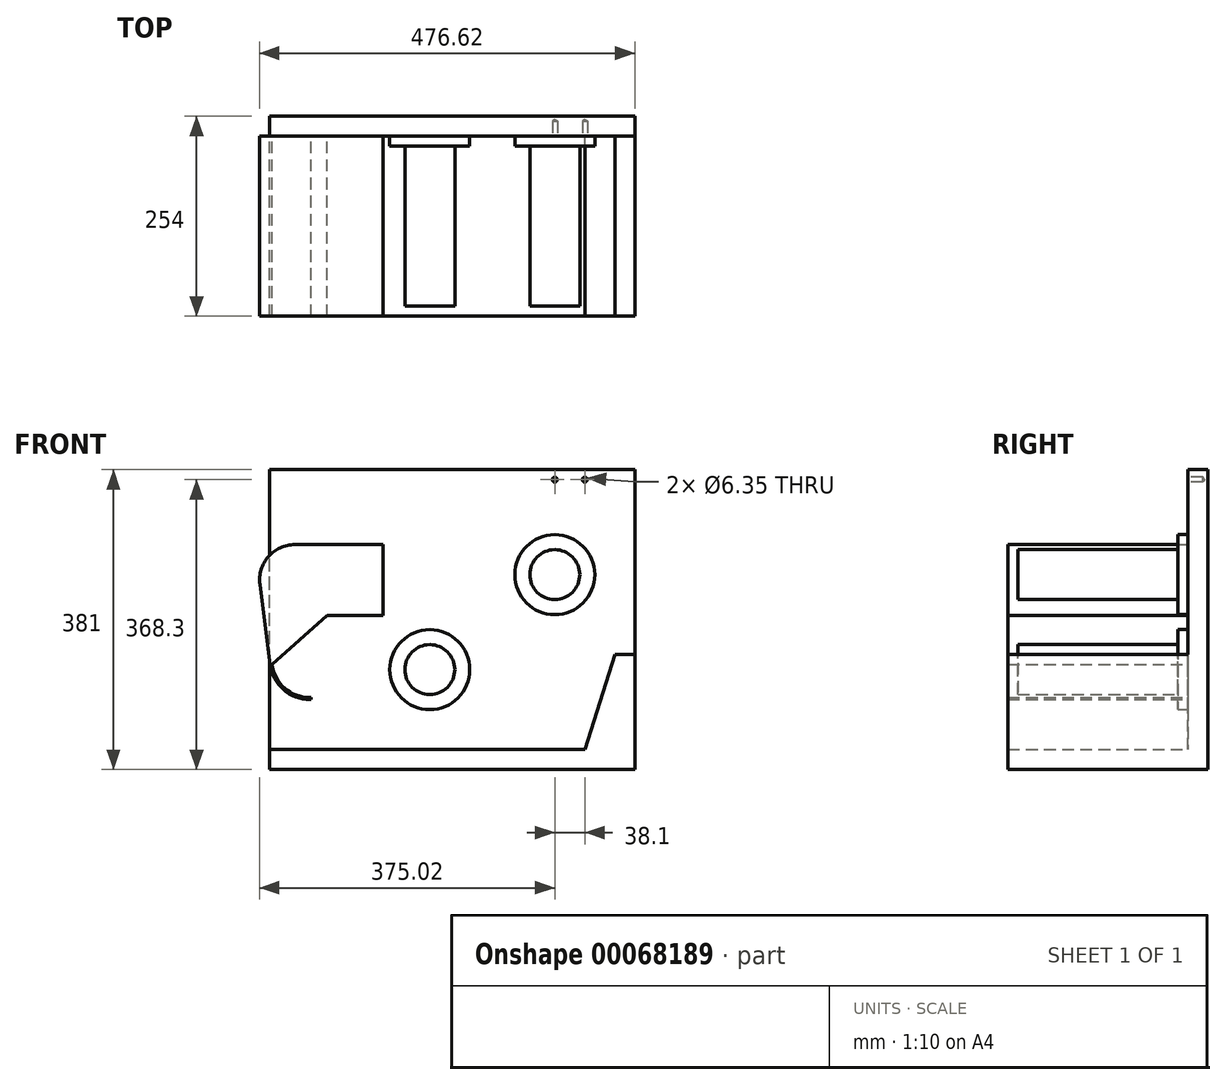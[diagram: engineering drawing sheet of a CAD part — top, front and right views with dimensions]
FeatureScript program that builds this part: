
annotation { "Feature Type Name" : "Feature", "Feature Type Description" : "" }
export const myFeature = defineFeature(function(context is Context, id is Id, definition is map)
    precondition{}
    {
        {
            var Q0;
            Q0=qCreatedBy(makeId("Front.planeOp"),FACE);
            var sketch = newSketch(context, id + "F0", { "sketchPlane" : qUnion([Q0])});
            skLineSegment(sketch, "E0.bottom", {"start": v(0, 0) * mm, "end": v(463.55, 0) * mm});
            skLineSegment(sketch, "E0.top", {"start": v(0, 381) * mm, "end": v(463.55, 381) * mm});
            skLineSegment(sketch, "E0.left", {"start": v(0, 0) * mm, "end": v(0, 381) * mm});
            skLineSegment(sketch, "E0.right", {"start": v(463.55, 0) * mm, "end": v(463.55, 381) * mm});
            skSolve(sketch);
        }
        {
            var Q0;
            Q0=makeQuery(id+"F0.imprint","IMPRINT",FACE,{"disambiguationData":[TD([[makeQuery(id+"F0.imprint","IMPRINT",EDGE,{"derivedFrom":sQuery(id+"F0.wireOp",EDGE,"E0.bottom")}),1.0]])]});
            extrude(context, id + "F1", {"entities" : qUnion([Q0]), "depth" : 25.4 * mm});
        }
        {
            var Q0;
            Q0=makeQuery(id+"F1.opExtrude","CAP_FACE",FACE,{"disambiguationData":[OSD([sQuery(id+"F0.wireOp",EDGE,"E0.bottom"),sQuery(id+"F0.wireOp",EDGE,"E0.top"),sQuery(id+"F0.wireOp",EDGE,"E0.left"),sQuery(id+"F0.wireOp",EDGE,"E0.right")])],"isStart":false});
            var sketch = newSketch(context, id + "F2", { "sketchPlane" : qUnion([Q0])});
            skLineSegment(sketch, "E1.bottom", {"start": v(0, 0) * mm, "end": v(463.55, 0) * mm});
            skLineSegment(sketch, "E1.top", {"start": v(0, 25.4) * mm, "end": v(463.55, 25.4) * mm});
            skLineSegment(sketch, "E1.left", {"start": v(0, 0) * mm, "end": v(0, 25.4) * mm});
            skLineSegment(sketch, "E1.right", {"start": v(463.55, 0) * mm, "end": v(463.55, 25.4) * mm});
            skSolve(sketch);
        }
        {
            var Q0;
            Q0=makeQuery(id+"F2.imprint","IMPRINT",FACE,{"disambiguationData":[TD([[makeQuery(id+"F2.imprint","IMPRINT",EDGE,{"derivedFrom":sQuery(id+"F2.wireOp",EDGE,"E1.bottom")}),1.0]])]});
            extrude(context, id + "F3", {"entities" : qUnion([Q0]), "operationType" : NewBodyOperationType.ADD, "depth" : 228.6 * mm});
        }
        {
            var Q0;
            Q0=makeQuery(id+"F1.opExtrude","CAP_FACE",FACE,{"disambiguationData":[OSD([sQuery(id+"F0.wireOp",EDGE,"E0.bottom"),sQuery(id+"F0.wireOp",EDGE,"E0.top"),sQuery(id+"F0.wireOp",EDGE,"E0.left"),sQuery(id+"F0.wireOp",EDGE,"E0.right")])],"isStart":false});
            var sketch = newSketch(context, id + "F4", { "sketchPlane" : qUnion([Q0])});
            skLineSegment(sketch, "E2", {"start": v(0.41, 133.22) * mm, "end": v(-12.7, 235.22) * mm});
            skArc(sketch, "E3", {"start": v(31.75, 285.75) * mm, "mid": v(-1.9, 270.53) * mm, "end": v(-12.7, 235.22) * mm});
            skArc(sketch, "E4", {"start": v(0.41, 133.22) * mm, "mid": v(17.25, 101.56) * mm, "end": v(50.8, 88.9) * mm});
            skLineSegment(sketch, "E5", {"start": v(31.75, 285.75) * mm, "end": v(144.01, 285.75) * mm});
            skLineSegment(sketch, "E6", {"start": v(144.01, 285.75) * mm, "end": v(144.01, 195.85) * mm});
            skLineSegment(sketch, "E7", {"start": v(144.01, 195.85) * mm, "end": v(72.48, 195.85) * mm});
            skLineSegment(sketch, "E8", {"start": v(50.8, 88.9) * mm, "end": v(50.8, 91.44) * mm});
            skArc(sketch, "E9", {"start": v(2.93, 133.55) * mm, "mid": v(18.93, 103.46) * mm, "end": v(50.8, 91.44) * mm});
            skLineSegment(sketch, "E10", {"start": v(50.8, 88.9) * mm, "end": v(50.8, 139.7) * mm, "construction": true});
            skLineSegment(sketch, "E11", {"start": v(0.41, 133.22) * mm, "end": v(50.8, 139.7) * mm, "construction": true});
            skLineSegment(sketch, "E12", {"start": v(2.93, 133.55) * mm, "end": v(72.48, 195.85) * mm});
            skSolve(sketch);
        }
        {
            var Q0;
            Q0 = qSketchRegion(id + "F4", true);
            var Q1;
            Q1=makeQuery(id+"F4.imprint","IMPRINT",FACE,{"disambiguationData":[TD([[makeQuery(id+"F4.imprint","IMPRINT",EDGE,{"derivedFrom":sQuery(id+"F4.wireOp",EDGE,"E2")}),-1.0]])]});
            extrude(context, id + "F5", {"entities" : qUnion([Q0, Q1]), "operationType" : NewBodyOperationType.ADD, "depth" : 228.6 * mm});
        }
        {
            var Q0;
            Q0=makeQuery(id+"F1.opExtrude","CAP_FACE",FACE,{"disambiguationData":[OSD([sQuery(id+"F0.wireOp",EDGE,"E0.bottom"),sQuery(id+"F0.wireOp",EDGE,"E0.top"),sQuery(id+"F0.wireOp",EDGE,"E0.left"),sQuery(id+"F0.wireOp",EDGE,"E0.right")])],"isStart":false});
            var sketch = newSketch(context, id + "F6", { "sketchPlane" : qUnion([Q0])});
            skPoint(sketch, "E13", {"position": v(361.95, 368.3) * mm});
            skPoint(sketch, "E14", {"position": v(400.05, 368.3) * mm});
            skSolve(sketch);
        }
        {
            var Q0;
            Q0=sQuery(id+"F6.wireOp",VERTEX,"E13");
            var Q1;
            Q1=sQuery(id+"F6.wireOp",VERTEX,"E14");
            var Q2;
            Q2=makeQuery(id+"F1.opExtrude","SWEPT_BODY",BODY,{"disambiguationData":[OSD([sQuery(id+"F0.wireOp",EDGE,"E0.bottom"),sQuery(id+"F0.wireOp",EDGE,"E0.top"),sQuery(id+"F0.wireOp",EDGE,"E0.left"),sQuery(id+"F0.wireOp",EDGE,"E0.right")])]});
            hole(context, id + "F7", {"style" : HoleStyle.SIMPLE, "holeDiameter" : 6.35 * mm, "endStyle" : HoleEndStyle.BLIND, "holeDepth" : 19.05 * mm, "locations" : qUnion([Q0, Q1]), "scope" : qUnion([Q2])});
        }
        {
            var Q0;
            Q0=makeQuery(id+"F5.opExtrude","SWEPT_FACE",FACE,{"disambiguationData":[OSD([sQuery(id+"F4.wireOp",EDGE,"E8")])]});
            extrude(context, id + "F8", {"entities" : qUnion([Q0]), "operationType" : NewBodyOperationType.ADD, "depth" : (1 + (7 / 8)) * mm});
        }
        {
            var Q0;
            Q0=makeQuery(id+"F1.opExtrude","CAP_FACE",FACE,{"disambiguationData":[OSD([sQuery(id+"F0.wireOp",EDGE,"E0.bottom"),sQuery(id+"F0.wireOp",EDGE,"E0.top"),sQuery(id+"F0.wireOp",EDGE,"E0.left"),sQuery(id+"F0.wireOp",EDGE,"E0.right")])],"isStart":false});
            var sketch = newSketch(context, id + "F9", { "sketchPlane" : qUnion([Q0])});
            skCircle(sketch, "E15", {"center": v(203.2, 127) * mm, "radius": 50.8 * mm});
            skSolve(sketch);
        }
        {
            var Q0;
            Q0 = qSketchRegion(id + "F9", true);
            extrude(context, id + "F10", {"entities" : qUnion([Q0]), "operationType" : NewBodyOperationType.ADD, "depth" : 12.7 * mm});
        }
        {
            var Q0;
            Q0=makeQuery(id+"F10.opExtrude","CAP_FACE",FACE,{"disambiguationData":[OSD([sQuery(id+"F9.wireOp",EDGE,"E15")])],"isStart":false});
            var sketch = newSketch(context, id + "F11", { "sketchPlane" : qUnion([Q0])});
            skCircle(sketch, "E16", {"center": v(203.2, 127) * mm, "radius": 31.75 * mm});
            skSolve(sketch);
        }
        {
            var Q0;
            Q0 = qSketchRegion(id + "F11", true);
            extrude(context, id + "F12", {"entities" : qUnion([Q0]), "operationType" : NewBodyOperationType.ADD, "depth" : 203.2 * mm});
        }
        {
            var Q0;
            Q0=makeQuery(id+"F1.opExtrude","CAP_FACE",FACE,{"disambiguationData":[OSD([sQuery(id+"F0.wireOp",EDGE,"E0.bottom"),sQuery(id+"F0.wireOp",EDGE,"E0.top"),sQuery(id+"F0.wireOp",EDGE,"E0.left"),sQuery(id+"F0.wireOp",EDGE,"E0.right")])],"isStart":false});
            var sketch = newSketch(context, id + "F13", { "sketchPlane" : qUnion([Q0])});
            skCircle(sketch, "E17", {"center": v(361.95, 247.65) * mm, "radius": 50.8 * mm});
            skSolve(sketch);
        }
        {
            var Q0;
            Q0 = qSketchRegion(id + "F13", true);
            extrude(context, id + "F14", {"entities" : qUnion([Q0]), "operationType" : NewBodyOperationType.ADD, "depth" : 12.7 * mm});
        }
        {
            var Q0;
            Q0=makeQuery(id+"F14.opExtrude","CAP_FACE",FACE,{"disambiguationData":[OSD([sQuery(id+"F13.wireOp",EDGE,"E17")])],"isStart":false});
            var sketch = newSketch(context, id + "F15", { "sketchPlane" : qUnion([Q0])});
            skCircle(sketch, "E18", {"center": v(361.95, 247.65) * mm, "radius": 31.75 * mm});
            skSolve(sketch);
        }
        {
            var Q0;
            Q0 = qSketchRegion(id + "F15", true);
            extrude(context, id + "F16", {"entities" : qUnion([Q0]), "operationType" : NewBodyOperationType.ADD, "depth" : 203.2 * mm});
        }
        {
            var Q0;
            Q0=makeQuery(id+"F1.opExtrude","CAP_FACE",FACE,{"disambiguationData":[OSD([sQuery(id+"F0.wireOp",EDGE,"E0.bottom"),sQuery(id+"F0.wireOp",EDGE,"E0.top"),sQuery(id+"F0.wireOp",EDGE,"E0.left"),sQuery(id+"F0.wireOp",EDGE,"E0.right")])],"isStart":false});
            var sketch = newSketch(context, id + "F17", { "sketchPlane" : qUnion([Q0])});
            skLineSegment(sketch, "E19", {"start": v(400.05, 25.4) * mm, "end": v(463.55, 25.4) * mm});
            skLineSegment(sketch, "E20", {"start": v(463.55, 25.4) * mm, "end": v(463.55, 146.05) * mm});
            skLineSegment(sketch, "E21", {"start": v(438.15, 146.05) * mm, "end": v(463.55, 146.05) * mm});
            skLineSegment(sketch, "E22", {"start": v(438.15, 146.05) * mm, "end": v(400.05, 25.4) * mm});
            skSolve(sketch);
        }
        {
            var Q0;
            Q0 = qSketchRegion(id + "F17", true);
            extrude(context, id + "F18", {"entities" : qUnion([Q0]), "operationType" : NewBodyOperationType.ADD, "depth" : 228.6 * mm});
        }
    });
